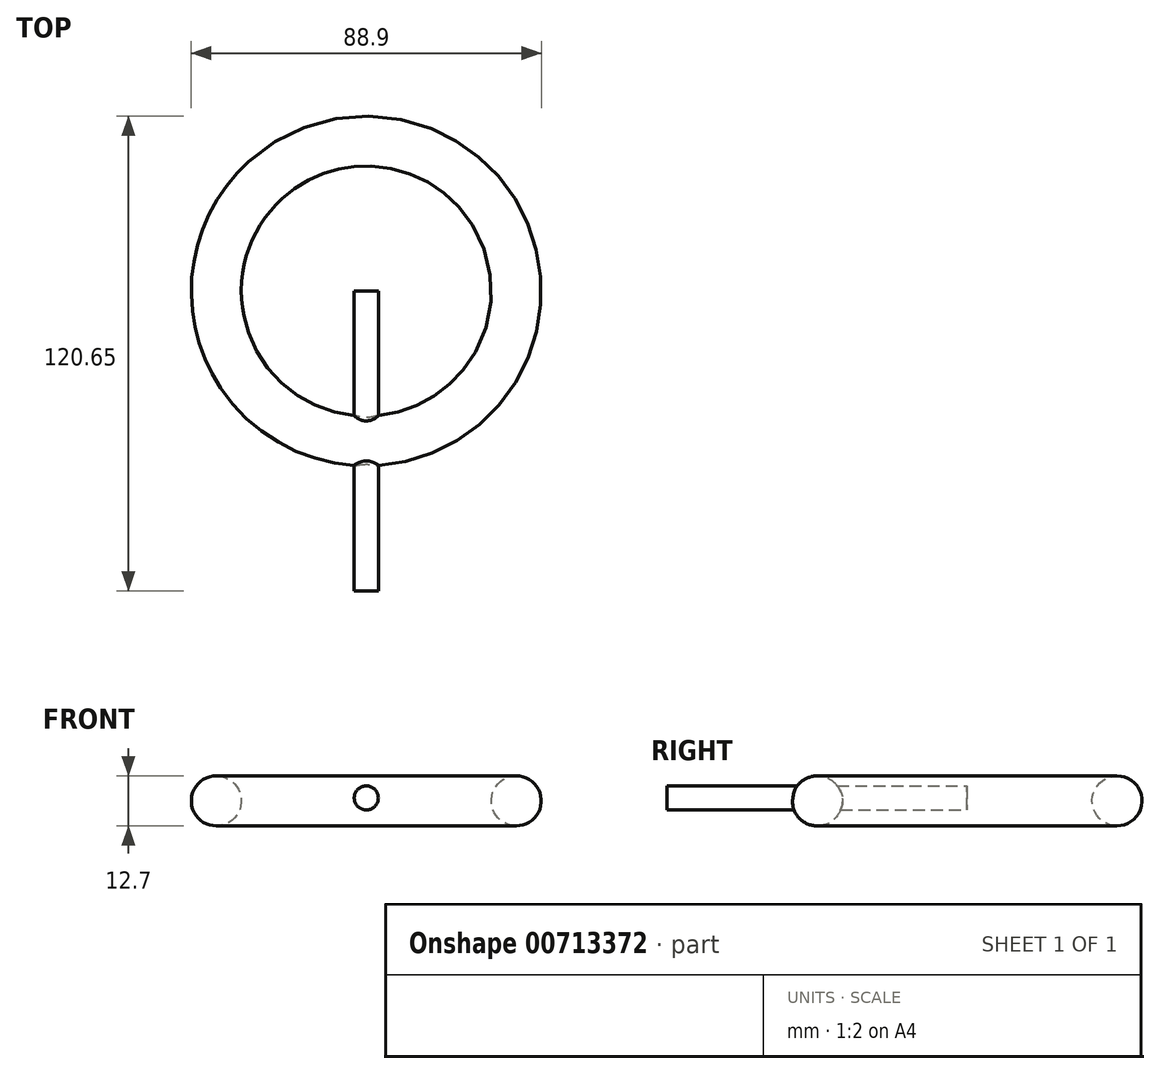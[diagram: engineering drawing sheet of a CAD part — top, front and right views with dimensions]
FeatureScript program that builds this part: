
annotation { "Feature Type Name" : "Feature", "Feature Type Description" : "" }
export const myFeature = defineFeature(function(context is Context, id is Id, definition is map)
    precondition{}
    {
        {
            var Q0;
            Q0=qCreatedBy(makeId("Front.planeOp"),FACE);
            var sketch = newSketch(context, id + "F0", { "sketchPlane" : qUnion([Q0])});
            skCircle(sketch, "E0", {"center": v(38.1, 9.95) * mm, "radius": 6.35 * mm});
            skLineSegment(sketch, "E1", {"start": v(38.1, 9.95) * mm, "end": v(0, 9.95) * mm});
            skLineSegment(sketch, "E2", {"start": v(0, 76.06) * mm, "end": v(0, -75.7) * mm});
            skSolve(sketch);
        }
        {
            var Q0;
            Q0=makeQuery(id+"F0.imprint","IMPRINT",FACE,{"disambiguationData":[TD([[makeQuery(id+"F0.imprint","IMPRINT",EDGE,{"derivedFrom":sQuery(id+"F0.wireOp",EDGE,"E0")}),1.0]])]});
            var Q1;
            Q1=sQuery(id+"F0.wireOp",EDGE,"E2");
            revolve(context, id + "F1", {"surfaceOperationType" : NewSurfaceOperationType.NEW, "entities" : qUnion([Q0]), "axis" : qUnion([Q1]), "revolveType" : RevolveType.FULL});
        }
        {
            var Q0;
            Q0=qCreatedBy(makeId("Front.planeOp"),FACE);
            var sketch = newSketch(context, id + "F2", { "sketchPlane" : qUnion([Q0])});
            skCircle(sketch, "E3", {"center": v(0, 10.7) * mm, "radius": 3.06 * mm});
            skSolve(sketch);
        }
        {
            var Q0;
            Q0 = qSketchRegion(id + "F2", true);
            extrude(context, id + "F3", {"entities" : qUnion([Q0]), "operationType" : NewBodyOperationType.ADD, "depth" : 76.2 * mm, "offsetDistance" : 25.4 * mm});
        }
    });
